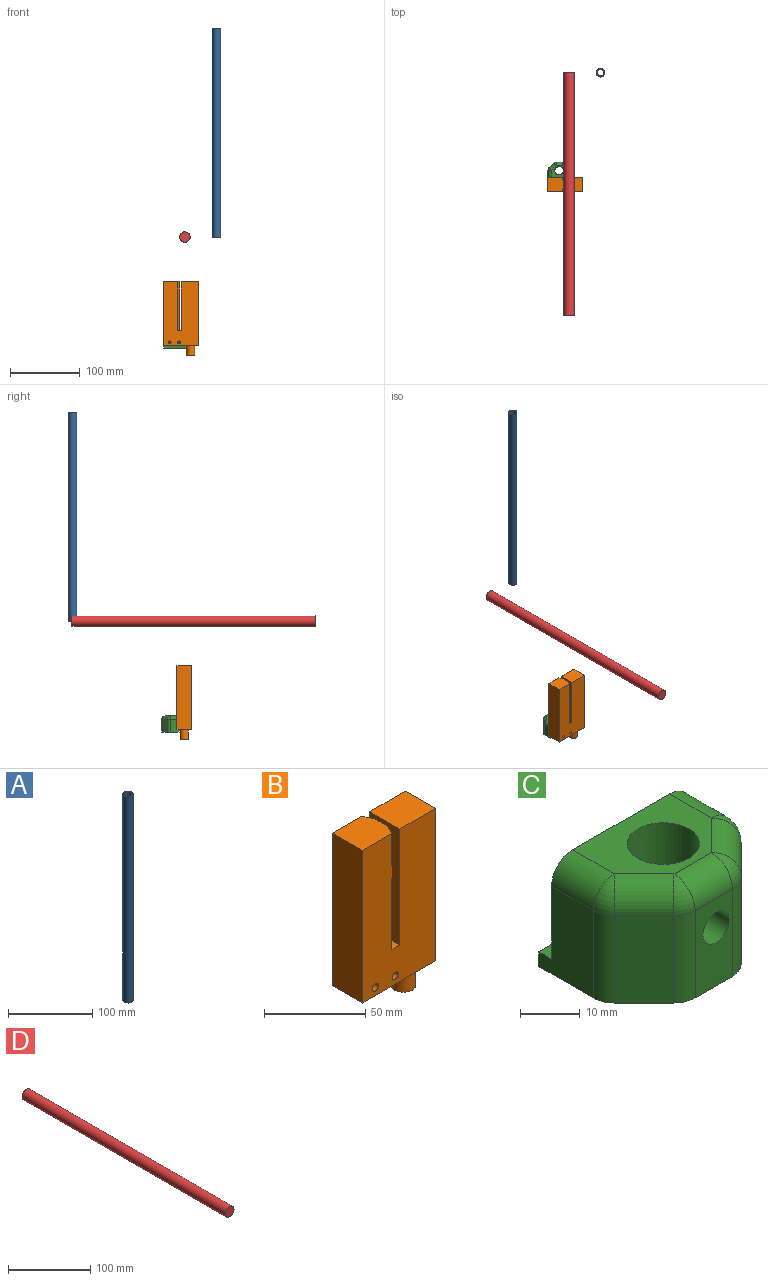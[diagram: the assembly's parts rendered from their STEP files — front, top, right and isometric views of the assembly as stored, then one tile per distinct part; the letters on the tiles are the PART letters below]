
ASSEMBLY  parts=4 mates=1
PART A: 4 faces, bbox 12x12x300 mm
  f0: cylinder r=5mm len=300mm, axis (0,0,-1), area 9424.8mm2, adj f2,f3
  f1: cylinder r=6mm len=300mm, axis (0,0,-1), area 11309.7mm2, adj f2,f3
  f2: plane 12x12mm, normal (0,0,1), area 34.6mm2, adj f0,f1
  f3: plane 12x12mm, normal (0,0,-1), area 34.6mm2, adj f0,f1
PART B: 16 faces, bbox 51x21x106 mm
  f0: plane 70x21mm, normal (-1,0,0), area 1470mm2, adj f1,f8,f10,f11
  f1: plane 21x5.5mm, normal (0,0,1), area 70.5mm2, adj f0,f2,f10,f11,f12,f13
  f2: plane 70x9mm, normal (1,0,0), area 630mm2, adj f1,f3,f12,f13
  f3: plane 23.5x21mm, normal (0,0,1), area 475.5mm2, adj f2,f4,f10,f11,f12,f13
  f4: plane 92x21mm, normal (-1,0,0), area 1932mm2, adj f3,f5,f10,f11
  f5: plane 51x21mm, normal (0,0,-1), area 957.9mm2, adj f4,f6,f10,f11,f14
  f6: plane 92x21mm, normal (1,0,0), area 1932mm2, adj f5,f8,f10,f11
  f7: cylinder r=2.15mm len=21mm, axis (0,1,0), area 283.7mm2, adj f10,f11
  f8: plane 25x21mm, normal (0,0,1), area 525mm2, adj f0,f6,f10,f11
  f9: cylinder r=2.15mm len=21mm, axis (0,1,0), area 283.7mm2, adj f10,f11
  f10: plane 92x51mm, normal (0,-1,0), area 4278mm2, adj f0,f1,f3,f4,f5,f6,f7,f8
  f11: plane 92x51mm, normal (0,1,0), area 4278mm2, adj f0,f1,f3,f4,f5,f6,f7,f8
  f12: plane 70x6mm, normal (0.89,0.45,0), area 469.6mm2, adj f1,f2,f3,f11
  f13: plane 70x6mm, normal (0.89,-0.45,0), area 469.6mm2, adj f1,f2,f3,f10
  f14: cylinder r=6mm len=14mm, axis (0,0,1), area 527.8mm2, adj f5,f15
  f15: plane 12x12mm, normal (0,0,-1), area 113.1mm2, adj f14
PART C: 31 faces, bbox 33x25x23 mm
  f0: plane 18x12.93mm, normal (-1,0,0), area 187.7mm2, adj f1,f2,f7,f8,f21,f22
  f1: plane 33x3mm, normal (0,1,0), area 99mm2, adj f0,f2,f3,f7
  f2: plane 33x25mm, normal (0,0,-1), area 607.9mm2, adj f0,f1,f3,f5,f6,f16,f17,f18
  f3: plane 18x12.93mm, normal (1,0,0), area 187.7mm2, adj f1,f2,f7,f8,f18,f30
  f4: plane 23x17mm, normal (0,0,1), area 226mm2, adj f6,f8,f22,f24,f26,f28,f30
  f5: plane 18x8.86mm, normal (0,-1,0), area 129.3mm2, adj f2,f15,f19,f20,f26
  f6: cylinder r=6.05mm len=23mm, axis (0,0,1), area 843mm2, adj f2,f4,f15
  f7: plane 33x3mm, normal (0,0,1), area 99mm2, adj f0,f1,f3,f8
  f8: plane 33x20mm, normal (0,1,0), area 632.2mm2, adj f0,f3,f4,f7,f10,f12,f22,f30
  f9: plane 0.9x0.9mm, normal (0,1,0), area 0.6mm2, adj f14
  f10: cylinder r=1.65mm len=3.8mm, axis (0,1,0), area 39.4mm2, adj f8,f14
  f11: plane 0.9x0.9mm, normal (0,1,0), area 0.6mm2, adj f13
  f12: cylinder r=1.65mm len=3.8mm, axis (0,1,0), area 39.4mm2, adj f8,f13
  f13: cone r=0.45mm half-angle=45deg, axis (0,1,0), area 11.2mm2, adj f11,f12
  f14: cone r=0.45mm half-angle=45deg, axis (0,1,0), area 11.2mm2, adj f9,f10
  f15: cylinder r=3.1mm len=7.31mm, axis (0,-1,0), area 133.8mm2, adj f5,f6
  f16: plane 18x7.07mm, normal (-0.71,-0.71,0), area 180mm2, adj f2,f19,f21,f24
  f17: plane 18x7.07mm, normal (0.71,-0.71,0), area 180mm2, adj f2,f18,f20,f28
  f18: cylinder r=5mm len=18mm, axis (0,0,1), area 70.7mm2, adj f2,f3,f17,f29
  f19: cylinder r=5mm len=18mm, axis (0,0,1), area 70.7mm2, adj f2,f5,f16,f25
  f20: cylinder r=5mm len=18mm, axis (0,0,1), area 70.7mm2, adj f2,f5,f17,f27
  f21: cylinder r=5mm len=18mm, axis (0,0,-1), area 70.7mm2, adj f0,f2,f16,f23
  f22: cylinder r=5mm len=9.93mm, axis (0,-1,0), area 78mm2, adj f0,f4,f8,f23
  f23: sphere r=5mm, area 19.6mm2, adj f21,f22,f24
  f24: cylinder r=5mm len=10.61mm, axis (0.71,-0.71,0), area 78.5mm2, adj f4,f16,f23,f25
  f25: sphere r=5mm, area 19.6mm2, adj f19,f24,f26
  f26: cylinder r=5mm len=8.86mm, axis (1,0,0), area 69.6mm2, adj f4,f5,f25,f27
  f27: sphere r=5mm, area 19.6mm2, adj f20,f26,f28
  f28: cylinder r=5mm len=10.61mm, axis (-0.71,-0.71,0), area 78.5mm2, adj f4,f17,f27,f29
  f29: sphere r=5mm, area 19.6mm2, adj f18,f28,f30
  f30: cylinder r=5mm len=9.93mm, axis (0,1,0), area 78mm2, adj f3,f4,f8,f29
PART D: 3 faces, bbox 15x350x15 mm
  f0: cylinder r=7.5mm len=350mm, axis (0,1,0), area 16493.4mm2, adj f1,f2
  f1: plane 15x15mm, normal (0,-1,0), area 176.7mm2, adj f0
  f2: plane 15x15mm, normal (0,1,0), area 176.7mm2, adj f0
PLACE A t=(53.69,186.55,150)mm
PLACE B t=(28.13,36.61,-6.45)mm
PLACE C rot(axis=(0,0,1),180deg) t=(-21.87,33.61,-9.45)mm
PLACE D t=(8.22,187.51,150)mm
MATE fastened C.f12 <-> B.f7  axis (0,-1,0) through (-13.87,36.61,-1.45)mm
